# Revit family: Plumbing_Drainage_Menzies-Metal_Clamp-Tite_Aluminum-Drain
name_source: partatom
category: Plumbing Fixtures
revit_build: Autodesk Revit 2015 (Build: 20160512_1515(x64)
units: mm (PartAtom-declared; Revit-internal decimal feet)

## types (5) — shared parameters
Assembly Code = D2040200
Default Elevation = 4' - 0"
Description = Clamp-Tite Spun Aluminum Drain
Drain Flow = 0 GPM
Edition number = 1
Manufacturer = Menzies Metal Products
Pipe Length = 0' - 11"
Pipe Length Note = Longer pipes available.  Pipes can be field cut to the desired length.
Product Guid = 59f602b9-b5f5-448c-8fc4-15881cd61602
Product Material = Metal - Menzies Metal Products - Aluminum
Product data url = https://bimobject.com
URL = https://www.menzies-metal.com

## per-type parameters (varying)
| type | Model | Weight |
| 2" | 300-3390 | 3.70 lbf |
| 3" | 300-3395 | 3.95 lbf |
| 4" | 300-3400 | 4.00 lbf |
| 5" | 300-3401 | 5.00 lbf |
| 6" | 300-3402 | 6.00 lbf |

note: column(s) folded — value = type name in every type: Pipe Diameter

## geometry (parser evidence)
native form markers: Sweep x3
no freeform markers — native parametric forms only
